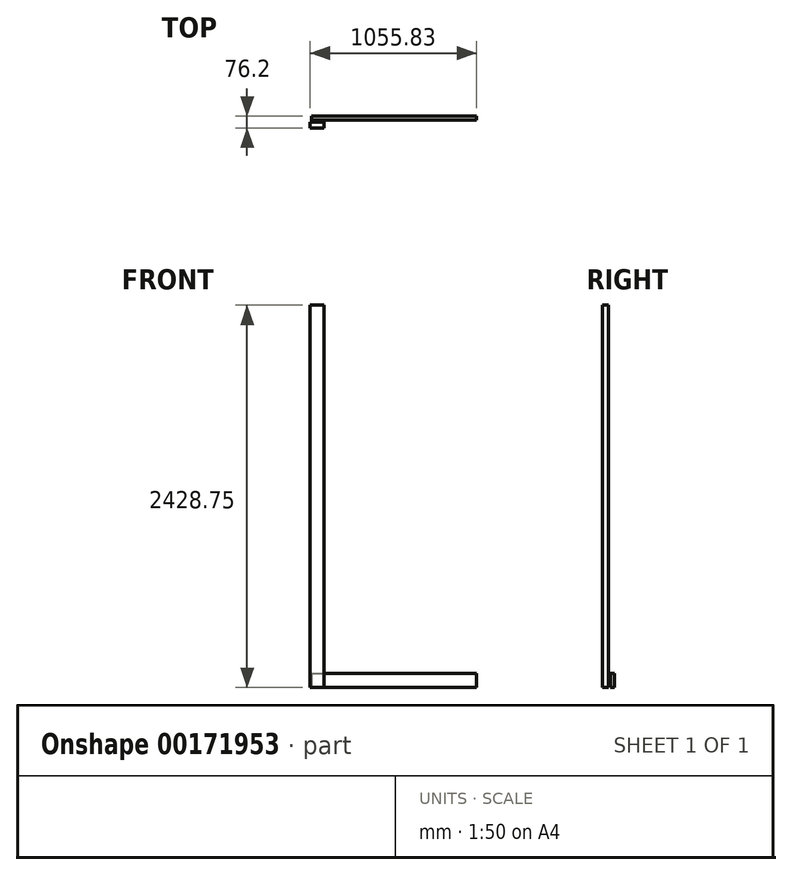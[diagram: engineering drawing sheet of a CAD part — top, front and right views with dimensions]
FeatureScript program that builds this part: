
annotation { "Feature Type Name" : "Feature", "Feature Type Description" : "" }
export const myFeature = defineFeature(function(context is Context, id is Id, definition is map)
    precondition{}
    {
        {
            var Q0;
            Q0=qCreatedBy(makeId("Front.planeOp"),FACE);
            var sketch = newSketch(context, id + "F0", { "sketchPlane" : qUnion([Q0])});
            skLineSegment(sketch, "E0.bottom", {"start": v(-242.18, 88.9) * mm, "end": v(805.57, 88.9) * mm});
            skLineSegment(sketch, "E0.top", {"start": v(-242.18, 0) * mm, "end": v(805.57, 0) * mm});
            skLineSegment(sketch, "E0.left", {"start": v(-242.18, 88.9) * mm, "end": v(-242.18, 0) * mm});
            skLineSegment(sketch, "E0.right", {"start": v(805.57, 88.9) * mm, "end": v(805.57, 0) * mm});
            skSolve(sketch);
        }
        {
            var Q0;
            Q0 = qSketchRegion(id + "F0", true);
            extrude(context, id + "F1", {"entities" : qUnion([Q0]), "depth" : 25.4 * mm});
        }
        {
            var Q0;
            Q0=qCreatedBy(makeId("Front.planeOp"),FACE);
            cPlane(context, id + "F2", {"entities" : qUnion([Q0]), "cplaneType" : CPlaneType.OFFSET, "offset" : 38.1 * mm, "width" : 152.4 * mm, "height" : 152.4 * mm});
        }
        {
            var Q0;
            Q0=qCreatedBy(id+"F2.planeOp",FACE);
            var sketch = newSketch(context, id + "F3", { "sketchPlane" : qUnion([Q0])});
            skLineSegment(sketch, "E1.bottom", {"start": v(-161.36, 0) * mm, "end": v(-250.26, 0) * mm});
            skLineSegment(sketch, "E1.top", {"start": v(-161.36, 2428.75) * mm, "end": v(-250.26, 2428.75) * mm});
            skLineSegment(sketch, "E1.left", {"start": v(-161.36, 0) * mm, "end": v(-161.36, 2428.75) * mm});
            skLineSegment(sketch, "E1.right", {"start": v(-250.26, 0) * mm, "end": v(-250.26, 2428.75) * mm});
            skSolve(sketch);
        }
        {
            var Q0;
            Q0 = qSketchRegion(id + "F3", true);
            extrude(context, id + "F4", {"entities" : qUnion([Q0]), "depth" : 38.1 * mm});
        }
    });
